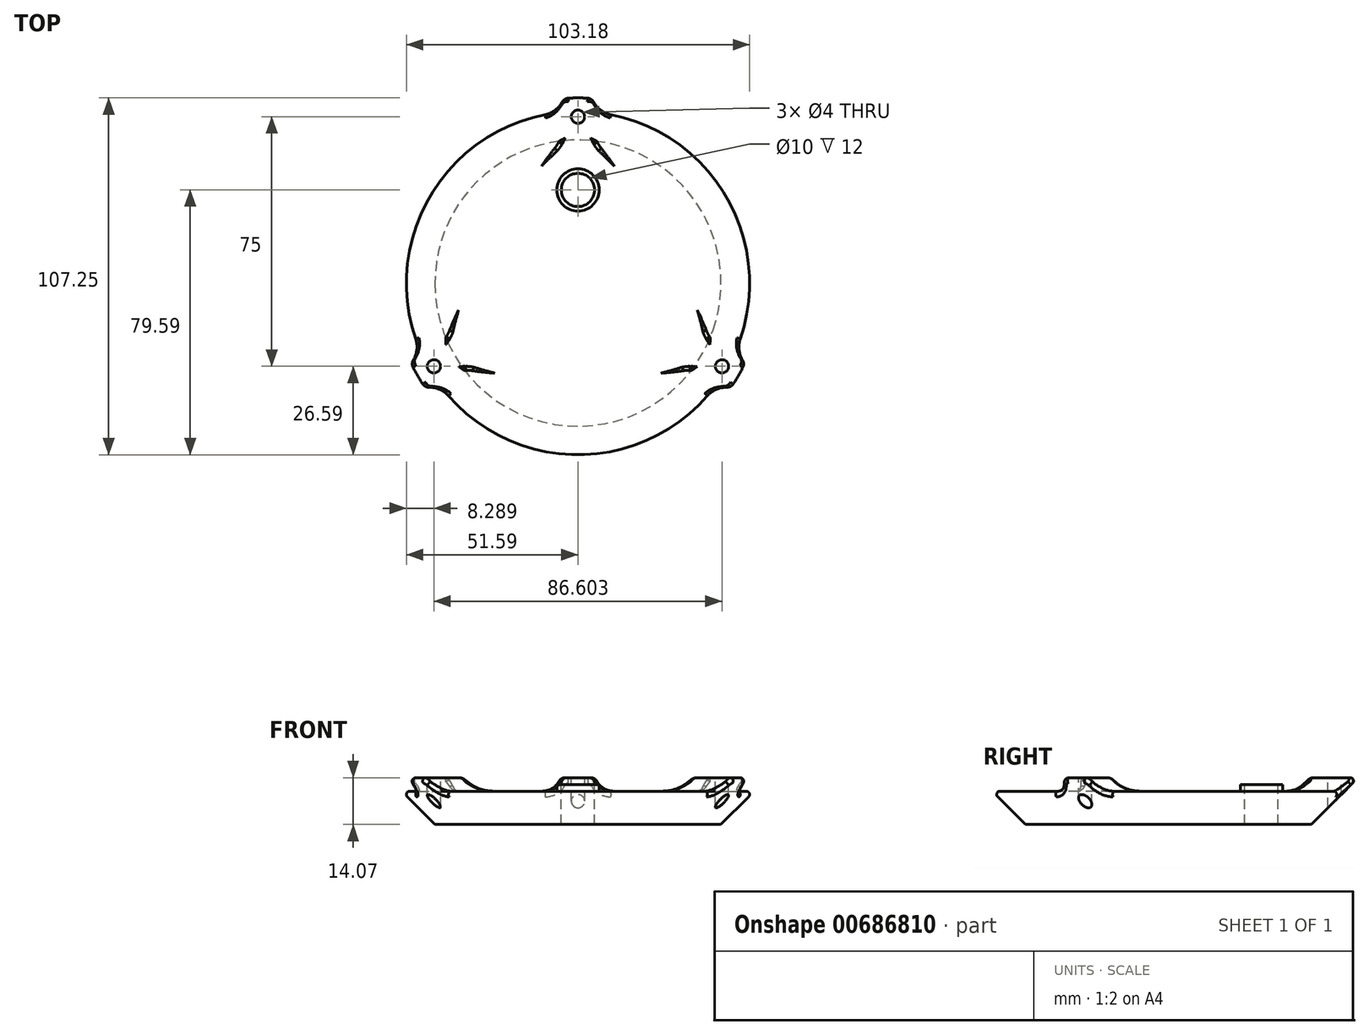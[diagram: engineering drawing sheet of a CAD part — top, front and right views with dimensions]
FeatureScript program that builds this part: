
annotation { "Feature Type Name" : "Feature", "Feature Type Description" : "" }
export const myFeature = defineFeature(function(context is Context, id is Id, definition is map)
    precondition{}
    {
        {
            var Q0;
            Q0=qCreatedBy(makeId("Front.planeOp"),FACE);
            var sketch = newSketch(context, id + "F0", { "sketchPlane" : qUnion([Q0])});
            skLineSegment(sketch, "E0", {"start": v(0, 0) * mm, "end": v(0, 10) * mm});
            skLineSegment(sketch, "E1", {"start": v(0, 10) * mm, "end": v(38.86, 10) * mm});
            skLineSegment(sketch, "E2", {"start": v(43, 0) * mm, "end": v(0, 0) * mm});
            skLineSegment(sketch, "E3", {"start": v(57.07, 14.07) * mm, "end": v(42.93, 14.07) * mm});
            skLineSegment(sketch, "E4", {"start": v(42.93, 14.07) * mm, "end": v(38.86, 10) * mm});
            skLineSegment(sketch, "E5", {"start": v(43, 0) * mm, "end": v(57.07, 14.07) * mm});
            skPoint(sketch, "E6", {"position": v(50, 14.07) * mm});
            skSolve(sketch);
        }
        {
            var Q0;
            Q0=makeQuery(id+"F0.imprint","IMPRINT",FACE,{"disambiguationData":[TD([[makeQuery(id+"F0.imprint","IMPRINT",EDGE,{"derivedFrom":sQuery(id+"F0.wireOp",EDGE,"E0")}),-1.0]])]});
            var Q1;
            Q1=sQuery(id+"F0.wireOp",EDGE,"E0");
            revolve(context, id + "F1", {"surfaceOperationType" : NewSurfaceOperationType.NEW, "entities" : qUnion([Q0]), "axis" : qUnion([Q1]), "revolveType" : RevolveType.FULL});
        }
        {
            var Q0;
            Q0=makeQuery(id+"F1.opRevolve","SWEPT_FACE",FACE,{"disambiguationData":[OSD([sQuery(id+"F0.wireOp",EDGE,"E3")])]});
            var sketch = newSketch(context, id + "F2", { "sketchPlane" : qUnion([Q0])});
            skCircle(sketch, "E7", {"center": v(0, 50) * mm, "radius": 2 * mm});
            skCircle(sketch, "E8.1.0", {"center": v(-43.3, -25) * mm, "radius": 2 * mm});
            skCircle(sketch, "E8.2.0", {"center": v(43.3, -25) * mm, "radius": 2 * mm});
            skPoint(sketch, "E8.center", {"position": v(0, 0) * mm});
            skSolve(sketch);
        }
        {
            var Q0;
            Q0 = qSketchRegion(id + "F2", true);
            extrude(context, id + "F3", {"entities" : qUnion([Q0]), "operationType" : NewBodyOperationType.REMOVE, "endBound" : BoundingType.UP_TO_NEXT, "oppositeDirection" : true, "depth" : 25 * mm, "offsetDistance" : 25 * mm});
        }
        {
            var Q0;
            Q0=makeQuery(id+"F1.opRevolve","SWEPT_FACE",FACE,{"disambiguationData":[OSD([sQuery(id+"F0.wireOp",EDGE,"E3")])]});
            var sketch = newSketch(context, id + "F4", { "sketchPlane" : qUnion([Q0])});
            skLineSegment(sketch, "E9", {"start": v(-4.12, 56.92) * mm, "end": v(-8.66, 5) * mm});
            skLineSegment(sketch, "E10", {"start": v(-8.66, 5) * mm, "end": v(-51.36, -24.9) * mm});
            skArc(sketch, "E11.0", {"start": v(-51.36, -24.9) * mm, "mid": v(-49.42, 28.54) * mm, "end": v(-4.12, 56.92) * mm});
            skLineSegment(sketch, "E12", {"start": v(0, 0) * mm, "end": v(0, 57.07) * mm, "construction": true});
            skLineSegment(sketch, "E13", {"start": v(0, 0) * mm, "end": v(-43.3, -25) * mm, "construction": true});
            skLineSegment(sketch, "E14.1.0", {"start": v(-47.24, -32.03) * mm, "end": v(0, -10) * mm});
            skArc(sketch, "E14.1.1", {"start": v(47.24, -32.03) * mm, "mid": v(0, -57.07) * mm, "end": v(-47.24, -32.03) * mm});
            skLineSegment(sketch, "E14.1.2", {"start": v(0, -10) * mm, "end": v(47.24, -32.03) * mm});
            skLineSegment(sketch, "E14.2.0", {"start": v(51.36, -24.9) * mm, "end": v(8.66, 5) * mm});
            skArc(sketch, "E14.2.1", {"start": v(4.12, 56.92) * mm, "mid": v(49.42, 28.54) * mm, "end": v(51.36, -24.9) * mm});
            skLineSegment(sketch, "E14.2.2", {"start": v(8.66, 5) * mm, "end": v(4.12, 56.92) * mm});
            skSolve(sketch);
        }
        {
            var Q0;
            Q0 = qSketchRegion(id + "F4", true);
            var Q1;
            Q1=makeQuery(id+"F1.opRevolve","SWEPT_FACE",FACE,{"disambiguationData":[OSD([sQuery(id+"F0.wireOp",EDGE,"E1")])]});
            extrude(context, id + "F5", {"entities" : qUnion([Q0]), "operationType" : NewBodyOperationType.REMOVE, "endBound" : BoundingType.UP_TO_SURFACE, "oppositeDirection" : true, "depth" : 25 * mm, "endBoundEntityFace" : qUnion([Q1]), "offsetDistance" : 25 * mm});
        }
        {
            var Q0;
            Q0=makeQuery(id+"F5.boolean.opBoolean","COPY",EDGE,{"derivedFrom":makeQuery(id+"F5.opExtrude","CAP_EDGE",EDGE,{"disambiguationData":[OSD([sQuery(id+"F4.wireOp",EDGE,"E9")])],"isStart":false})});
            var Q1;
            Q1=makeQuery(id+"F5.boolean.opBoolean","COPY",EDGE,{"derivedFrom":makeQuery(id+"F5.opExtrude","CAP_EDGE",EDGE,{"disambiguationData":[OSD([sQuery(id+"F4.wireOp",EDGE,"E14.2.2")])],"isStart":false})});
            var Q2;
            Q2=makeQuery(id+"F5.boolean.opBoolean","COPY",EDGE,{"derivedFrom":makeQuery(id+"F5.opExtrude","CAP_EDGE",EDGE,{"disambiguationData":[OSD([sQuery(id+"F4.wireOp",EDGE,"E14.2.0")])],"isStart":false})});
            var Q3;
            Q3=makeQuery(id+"F5.boolean.opBoolean","COPY",EDGE,{"derivedFrom":makeQuery(id+"F5.opExtrude","CAP_EDGE",EDGE,{"disambiguationData":[OSD([sQuery(id+"F4.wireOp",EDGE,"E14.1.2")])],"isStart":false})});
            var Q4;
            Q4=makeQuery(id+"F5.boolean.opBoolean","COPY",EDGE,{"derivedFrom":makeQuery(id+"F5.opExtrude","CAP_EDGE",EDGE,{"disambiguationData":[OSD([sQuery(id+"F4.wireOp",EDGE,"E14.1.0")])],"isStart":false})});
            var Q5;
            Q5=makeQuery(id+"F5.boolean.opBoolean","COPY",EDGE,{"derivedFrom":makeQuery(id+"F5.opExtrude","CAP_EDGE",EDGE,{"disambiguationData":[OSD([sQuery(id+"F4.wireOp",EDGE,"E10")])],"isStart":false})});
            var Q6;
            {var subQ0=sQuery(id+"F4.wireOp",EDGE,"E14.1.2");var subQ1=sQuery(id+"F0.wireOp",EDGE,"E4");var subQ2=sQuery(id+"F0.wireOp",EDGE,"E1");Q6=makeQuery(id+"F5.boolean.opBoolean","SPLIT",EDGE,{"disambiguationData":[TD([makeQuery(id+"F5.opExtrude","SWEPT_FACE",FACE,{"disambiguationData":[OSD([subQ0])]})])],"derivedFrom":makeQuery(id+"F1.opRevolve","SWEPT_EDGE",EDGE,{"disambiguationData":[OSD([subQ2,subQ1])]})});}
            var Q7;
            {var subQ0=sQuery(id+"F4.wireOp",EDGE,"E10");var subQ1=sQuery(id+"F0.wireOp",EDGE,"E4");var subQ2=sQuery(id+"F0.wireOp",EDGE,"E1");Q7=makeQuery(id+"F5.boolean.opBoolean","SPLIT",EDGE,{"disambiguationData":[TD([makeQuery(id+"F5.opExtrude","SWEPT_FACE",FACE,{"disambiguationData":[OSD([subQ0])]})])],"derivedFrom":makeQuery(id+"F1.opRevolve","SWEPT_EDGE",EDGE,{"disambiguationData":[OSD([subQ2,subQ1])]})});}
            var Q8;
            {var subQ0=sQuery(id+"F4.wireOp",EDGE,"E9");var subQ1=sQuery(id+"F0.wireOp",EDGE,"E4");var subQ2=sQuery(id+"F0.wireOp",EDGE,"E1");Q8=makeQuery(id+"F5.boolean.opBoolean","SPLIT",EDGE,{"disambiguationData":[TD([makeQuery(id+"F5.opExtrude","SWEPT_FACE",FACE,{"disambiguationData":[OSD([subQ0])]})])],"derivedFrom":makeQuery(id+"F1.opRevolve","SWEPT_EDGE",EDGE,{"disambiguationData":[OSD([subQ2,subQ1])]})});}
            fillet(context, id + "F6", {"entities" : qUnion([Q0, Q1, Q2, Q3, Q4, Q5, Q6, Q7, Q8]), "radius" : 5 * mm, "tangentPropagation" : true, "allowEdgeOverflow" : false});
        }
        {
            var Q0;
            Q0=makeQuery(id+"F5.boolean.opBoolean","INTERSECT",EDGE,{"derivedFrom":[makeQuery(id+"F1.opRevolve","SWEPT_FACE",FACE,{"disambiguationData":[OSD([sQuery(id+"F0.wireOp",EDGE,"E5")])]}),makeQuery(id+"F5.opExtrude","CAP_FACE",FACE,{"disambiguationData":[OSD([sQuery(id+"F4.wireOp",EDGE,"E14.2.0"),sQuery(id+"F4.wireOp",EDGE,"E14.2.1"),sQuery(id+"F4.wireOp",EDGE,"E14.2.2")])],"isStart":false})]});
            var Q1;
            Q1=makeQuery(id+"F5.boolean.opBoolean","INTERSECT",EDGE,{"derivedFrom":[makeQuery(id+"F1.opRevolve","SWEPT_FACE",FACE,{"disambiguationData":[OSD([sQuery(id+"F0.wireOp",EDGE,"E5")])]}),makeQuery(id+"F5.opExtrude","CAP_FACE",FACE,{"disambiguationData":[OSD([sQuery(id+"F4.wireOp",EDGE,"E9"),sQuery(id+"F4.wireOp",EDGE,"E10"),sQuery(id+"F4.wireOp",EDGE,"E11.0")])],"isStart":false})]});
            var Q2;
            Q2=makeQuery(id+"F5.boolean.opBoolean","INTERSECT",EDGE,{"derivedFrom":[makeQuery(id+"F1.opRevolve","SWEPT_FACE",FACE,{"disambiguationData":[OSD([sQuery(id+"F0.wireOp",EDGE,"E5")])]}),makeQuery(id+"F5.opExtrude","CAP_FACE",FACE,{"disambiguationData":[OSD([sQuery(id+"F4.wireOp",EDGE,"E14.1.0"),sQuery(id+"F4.wireOp",EDGE,"E14.1.1"),sQuery(id+"F4.wireOp",EDGE,"E14.1.2")])],"isStart":false})]});
            var Q3;
            {var subQ0=sQuery(id+"F4.wireOp",EDGE,"E10");Q3=makeQuery(id+"F6.opFillet","BLEND_EDGE",EDGE,{"blendedFrom":[makeQuery(id+"F5.boolean.opBoolean","COPY",EDGE,{"derivedFrom":makeQuery(id+"F5.opExtrude","CAP_EDGE",EDGE,{"disambiguationData":[OSD([subQ0])],"isStart":false})}),makeQuery(id+"F5.boolean.opBoolean","SPLIT",FACE,{"disambiguationData":[TD([makeQuery(id+"F5.opExtrude","SWEPT_FACE",FACE,{"disambiguationData":[OSD([subQ0])]})])],"derivedFrom":makeQuery(id+"F1.opRevolve","SWEPT_FACE",FACE,{"disambiguationData":[OSD([sQuery(id+"F0.wireOp",EDGE,"E4")])]})})],"blendedInto":[makeQuery(id+"F5.boolean.opBoolean","SPLIT",FACE,{"disambiguationData":[TD([makeQuery(id+"F5.opExtrude","SWEPT_FACE",FACE,{"disambiguationData":[OSD([subQ0])]})])],"derivedFrom":makeQuery(id+"F1.opRevolve","SWEPT_FACE",FACE,{"disambiguationData":[OSD([sQuery(id+"F0.wireOp",EDGE,"E4")])]})})]});}
            var Q4;
            {var subQ0=sQuery(id+"F4.wireOp",EDGE,"E10");var subQ1=sQuery(id+"F4.wireOp",EDGE,"E14.1.0");Q4=makeQuery(id+"F6.opFillet","BLEND_EDGE",EDGE,{"blendedFrom":[makeQuery(id+"F5.boolean.opBoolean","COPY",EDGE,{"derivedFrom":makeQuery(id+"F5.opExtrude","CAP_EDGE",EDGE,{"disambiguationData":[OSD([subQ1])],"isStart":false})}),makeQuery(id+"F5.boolean.opBoolean","SPLIT",FACE,{"disambiguationData":[TD([makeQuery(id+"F5.opExtrude","SWEPT_FACE",FACE,{"disambiguationData":[OSD([subQ0])]})])],"derivedFrom":makeQuery(id+"F1.opRevolve","SWEPT_FACE",FACE,{"disambiguationData":[OSD([sQuery(id+"F0.wireOp",EDGE,"E4")])]})})],"blendedInto":[makeQuery(id+"F5.boolean.opBoolean","SPLIT",FACE,{"disambiguationData":[TD([makeQuery(id+"F5.opExtrude","SWEPT_FACE",FACE,{"disambiguationData":[OSD([subQ0])]})])],"derivedFrom":makeQuery(id+"F1.opRevolve","SWEPT_FACE",FACE,{"disambiguationData":[OSD([sQuery(id+"F0.wireOp",EDGE,"E4")])]})})]});}
            var Q5;
            {var subQ0=sQuery(id+"F4.wireOp",EDGE,"E14.1.2");Q5=makeQuery(id+"F6.opFillet","BLEND_EDGE",EDGE,{"blendedFrom":[makeQuery(id+"F5.boolean.opBoolean","COPY",EDGE,{"derivedFrom":makeQuery(id+"F5.opExtrude","CAP_EDGE",EDGE,{"disambiguationData":[OSD([subQ0])],"isStart":false})}),makeQuery(id+"F5.boolean.opBoolean","SPLIT",FACE,{"disambiguationData":[TD([makeQuery(id+"F5.opExtrude","SWEPT_FACE",FACE,{"disambiguationData":[OSD([subQ0])]})])],"derivedFrom":makeQuery(id+"F1.opRevolve","SWEPT_FACE",FACE,{"disambiguationData":[OSD([sQuery(id+"F0.wireOp",EDGE,"E4")])]})})],"blendedInto":[makeQuery(id+"F5.boolean.opBoolean","SPLIT",FACE,{"disambiguationData":[TD([makeQuery(id+"F5.opExtrude","SWEPT_FACE",FACE,{"disambiguationData":[OSD([subQ0])]})])],"derivedFrom":makeQuery(id+"F1.opRevolve","SWEPT_FACE",FACE,{"disambiguationData":[OSD([sQuery(id+"F0.wireOp",EDGE,"E4")])]})})]});}
            var Q6;
            {var subQ0=sQuery(id+"F4.wireOp",EDGE,"E14.1.2");var subQ1=sQuery(id+"F4.wireOp",EDGE,"E14.2.0");Q6=makeQuery(id+"F6.opFillet","BLEND_EDGE",EDGE,{"blendedFrom":[makeQuery(id+"F5.boolean.opBoolean","COPY",EDGE,{"derivedFrom":makeQuery(id+"F5.opExtrude","CAP_EDGE",EDGE,{"disambiguationData":[OSD([subQ1])],"isStart":false})}),makeQuery(id+"F5.boolean.opBoolean","SPLIT",FACE,{"disambiguationData":[TD([makeQuery(id+"F5.opExtrude","SWEPT_FACE",FACE,{"disambiguationData":[OSD([subQ0])]})])],"derivedFrom":makeQuery(id+"F1.opRevolve","SWEPT_FACE",FACE,{"disambiguationData":[OSD([sQuery(id+"F0.wireOp",EDGE,"E4")])]})})],"blendedInto":[makeQuery(id+"F5.boolean.opBoolean","SPLIT",FACE,{"disambiguationData":[TD([makeQuery(id+"F5.opExtrude","SWEPT_FACE",FACE,{"disambiguationData":[OSD([subQ0])]})])],"derivedFrom":makeQuery(id+"F1.opRevolve","SWEPT_FACE",FACE,{"disambiguationData":[OSD([sQuery(id+"F0.wireOp",EDGE,"E4")])]})})]});}
            var Q7;
            {var subQ0=sQuery(id+"F4.wireOp",EDGE,"E9");var subQ1=sQuery(id+"F4.wireOp",EDGE,"E14.2.2");Q7=makeQuery(id+"F6.opFillet","BLEND_EDGE",EDGE,{"blendedFrom":[makeQuery(id+"F5.boolean.opBoolean","COPY",EDGE,{"derivedFrom":makeQuery(id+"F5.opExtrude","CAP_EDGE",EDGE,{"disambiguationData":[OSD([subQ1])],"isStart":false})}),makeQuery(id+"F5.boolean.opBoolean","SPLIT",FACE,{"disambiguationData":[TD([makeQuery(id+"F5.opExtrude","SWEPT_FACE",FACE,{"disambiguationData":[OSD([subQ0])]})])],"derivedFrom":makeQuery(id+"F1.opRevolve","SWEPT_FACE",FACE,{"disambiguationData":[OSD([sQuery(id+"F0.wireOp",EDGE,"E4")])]})})],"blendedInto":[makeQuery(id+"F5.boolean.opBoolean","SPLIT",FACE,{"disambiguationData":[TD([makeQuery(id+"F5.opExtrude","SWEPT_FACE",FACE,{"disambiguationData":[OSD([subQ0])]})])],"derivedFrom":makeQuery(id+"F1.opRevolve","SWEPT_FACE",FACE,{"disambiguationData":[OSD([sQuery(id+"F0.wireOp",EDGE,"E4")])]})})]});}
            var Q8;
            {var subQ0=sQuery(id+"F4.wireOp",EDGE,"E9");Q8=makeQuery(id+"F6.opFillet","BLEND_EDGE",EDGE,{"blendedFrom":[makeQuery(id+"F5.boolean.opBoolean","COPY",EDGE,{"derivedFrom":makeQuery(id+"F5.opExtrude","CAP_EDGE",EDGE,{"disambiguationData":[OSD([subQ0])],"isStart":false})}),makeQuery(id+"F5.boolean.opBoolean","SPLIT",FACE,{"disambiguationData":[TD([makeQuery(id+"F5.opExtrude","SWEPT_FACE",FACE,{"disambiguationData":[OSD([subQ0])]})])],"derivedFrom":makeQuery(id+"F1.opRevolve","SWEPT_FACE",FACE,{"disambiguationData":[OSD([sQuery(id+"F0.wireOp",EDGE,"E4")])]})})],"blendedInto":[makeQuery(id+"F5.boolean.opBoolean","SPLIT",FACE,{"disambiguationData":[TD([makeQuery(id+"F5.opExtrude","SWEPT_FACE",FACE,{"disambiguationData":[OSD([subQ0])]})])],"derivedFrom":makeQuery(id+"F1.opRevolve","SWEPT_FACE",FACE,{"disambiguationData":[OSD([sQuery(id+"F0.wireOp",EDGE,"E4")])]})})]});}
            var Q9;
            {var subQ0=sQuery(id+"F0.wireOp",EDGE,"E3");var subQ1=sQuery(id+"F0.wireOp",EDGE,"E5");Q9=makeQuery(id+"F5.boolean.opBoolean","SPLIT",EDGE,{"disambiguationData":[TD([makeQuery(id+"F5.opExtrude","SWEPT_FACE",FACE,{"disambiguationData":[OSD([sQuery(id+"F4.wireOp",EDGE,"E9")])]})])],"derivedFrom":makeQuery(id+"F1.opRevolve","SWEPT_EDGE",EDGE,{"disambiguationData":[OSD([subQ0,subQ1])]})});}
            var Q10;
            {var subQ0=sQuery(id+"F0.wireOp",EDGE,"E3");var subQ1=sQuery(id+"F0.wireOp",EDGE,"E5");Q10=makeQuery(id+"F5.boolean.opBoolean","SPLIT",EDGE,{"disambiguationData":[TD([makeQuery(id+"F5.opExtrude","SWEPT_FACE",FACE,{"disambiguationData":[OSD([sQuery(id+"F4.wireOp",EDGE,"E14.1.2")])]})])],"derivedFrom":makeQuery(id+"F1.opRevolve","SWEPT_EDGE",EDGE,{"disambiguationData":[OSD([subQ0,subQ1])]})});}
            var Q11;
            {var subQ0=sQuery(id+"F0.wireOp",EDGE,"E3");var subQ1=sQuery(id+"F0.wireOp",EDGE,"E5");Q11=makeQuery(id+"F5.boolean.opBoolean","SPLIT",EDGE,{"disambiguationData":[TD([makeQuery(id+"F5.opExtrude","SWEPT_FACE",FACE,{"disambiguationData":[OSD([sQuery(id+"F4.wireOp",EDGE,"E10")])]})])],"derivedFrom":makeQuery(id+"F1.opRevolve","SWEPT_EDGE",EDGE,{"disambiguationData":[OSD([subQ0,subQ1])]})});}
            fillet(context, id + "F7", {"entities" : qUnion([Q0, Q1, Q2, Q3, Q4, Q5, Q6, Q7, Q8, Q9, Q10, Q11]), "radius" : 1 * mm, "tangentPropagation" : true, "allowEdgeOverflow" : false});
        }
        {
            var Q0;
            {var subQ0=sQuery(id+"F4.wireOp",EDGE,"E9");Q0=makeQuery(id+"F6.opFillet","BLEND_EDGE",EDGE,{"blendedFrom":[makeQuery(id+"F5.boolean.opBoolean","COPY",EDGE,{"derivedFrom":makeQuery(id+"F5.opExtrude","CAP_EDGE",EDGE,{"disambiguationData":[OSD([subQ0])],"isStart":false})}),makeQuery(id+"F5.boolean.opBoolean","SPLIT",FACE,{"disambiguationData":[TD([makeQuery(id+"F3.boolean.opBoolean","COPY",FACE,{"derivedFrom":makeQuery(id+"F3.opExtrude","SWEPT_FACE",FACE,{"disambiguationData":[OSD([sQuery(id+"F2.wireOp",EDGE,"E7")])]})})])],"derivedFrom":makeQuery(id+"F1.opRevolve","SWEPT_FACE",FACE,{"disambiguationData":[OSD([sQuery(id+"F0.wireOp",EDGE,"E3")])]})})],"blendedInto":[makeQuery(id+"F5.boolean.opBoolean","SPLIT",FACE,{"disambiguationData":[TD([makeQuery(id+"F3.boolean.opBoolean","COPY",FACE,{"derivedFrom":makeQuery(id+"F3.opExtrude","SWEPT_FACE",FACE,{"disambiguationData":[OSD([sQuery(id+"F2.wireOp",EDGE,"E7")])]})})])],"derivedFrom":makeQuery(id+"F1.opRevolve","SWEPT_FACE",FACE,{"disambiguationData":[OSD([sQuery(id+"F0.wireOp",EDGE,"E3")])]})})]});}
            var Q1;
            {var subQ0=sQuery(id+"F0.wireOp",EDGE,"E3");var subQ1=sQuery(id+"F0.wireOp",EDGE,"E4");Q1=makeQuery(id+"F5.boolean.opBoolean","SPLIT",EDGE,{"disambiguationData":[TD([makeQuery(id+"F5.opExtrude","SWEPT_FACE",FACE,{"disambiguationData":[OSD([sQuery(id+"F4.wireOp",EDGE,"E14.1.2")])]})])],"derivedFrom":makeQuery(id+"F1.opRevolve","SWEPT_EDGE",EDGE,{"disambiguationData":[OSD([subQ0,subQ1])]})});}
            var Q2;
            {var subQ0=sQuery(id+"F0.wireOp",EDGE,"E3");var subQ1=sQuery(id+"F0.wireOp",EDGE,"E4");Q2=makeQuery(id+"F5.boolean.opBoolean","SPLIT",EDGE,{"disambiguationData":[TD([makeQuery(id+"F5.opExtrude","SWEPT_FACE",FACE,{"disambiguationData":[OSD([sQuery(id+"F4.wireOp",EDGE,"E10")])]})])],"derivedFrom":makeQuery(id+"F1.opRevolve","SWEPT_EDGE",EDGE,{"disambiguationData":[OSD([subQ0,subQ1])]})});}
            fillet(context, id + "F8", {"entities" : qUnion([Q0, Q1, Q2]), "radius" : 2 * mm, "tangentPropagation" : true, "allowEdgeOverflow" : false});
        }
        {
            var Q0;
            Q0=makeQuery(id+"F5.boolean.opBoolean","MERGE",FACE,{"derivedFrom":[makeQuery(id+"F1.opRevolve","SWEPT_FACE",FACE,{"disambiguationData":[OSD([sQuery(id+"F0.wireOp",EDGE,"E1")])]})],"fromTools":[makeQuery(id+"F5.opExtrude","CAP_FACE",FACE,{"disambiguationData":[OSD([sQuery(id+"F4.wireOp",EDGE,"E9"),sQuery(id+"F4.wireOp",EDGE,"E10"),sQuery(id+"F4.wireOp",EDGE,"E11.0")])],"isStart":false}),makeQuery(id+"F5.opExtrude","CAP_FACE",FACE,{"disambiguationData":[OSD([sQuery(id+"F4.wireOp",EDGE,"E14.1.0"),sQuery(id+"F4.wireOp",EDGE,"E14.1.1"),sQuery(id+"F4.wireOp",EDGE,"E14.1.2")])],"isStart":false}),makeQuery(id+"F5.opExtrude","CAP_FACE",FACE,{"disambiguationData":[OSD([sQuery(id+"F4.wireOp",EDGE,"E14.2.0"),sQuery(id+"F4.wireOp",EDGE,"E14.2.1"),sQuery(id+"F4.wireOp",EDGE,"E14.2.2")])],"isStart":false})]});
            var sketch = newSketch(context, id + "F9", { "sketchPlane" : qUnion([Q0])});
            skCircle(sketch, "E15", {"center": v(0, 28) * mm, "radius": 6.35 * mm});
            skSolve(sketch);
        }
        {
            var Q0;
            Q0 = qSketchRegion(id + "F9", true);
            extrude(context, id + "F10", {"entities" : qUnion([Q0]), "operationType" : NewBodyOperationType.ADD, "depth" : 2 * mm, "offsetDistance" : 25 * mm});
        }
        {
            var Q0;
            Q0=makeQuery(id+"F10.opExtrude","CAP_FACE",FACE,{"disambiguationData":[OSD([sQuery(id+"F9.wireOp",EDGE,"E15")])],"isStart":false});
            var sketch = newSketch(context, id + "F11", { "sketchPlane" : qUnion([Q0])});
            skCircle(sketch, "E16", {"center": v(0, 28) * mm, "radius": 5 * mm});
            skSolve(sketch);
        }
        {
            var Q0;
            Q0 = qSketchRegion(id + "F11", true);
            extrude(context, id + "F12", {"entities" : qUnion([Q0]), "operationType" : NewBodyOperationType.REMOVE, "endBound" : BoundingType.UP_TO_NEXT, "oppositeDirection" : true, "depth" : 25 * mm, "offsetDistance" : 25 * mm});
        }
    });
